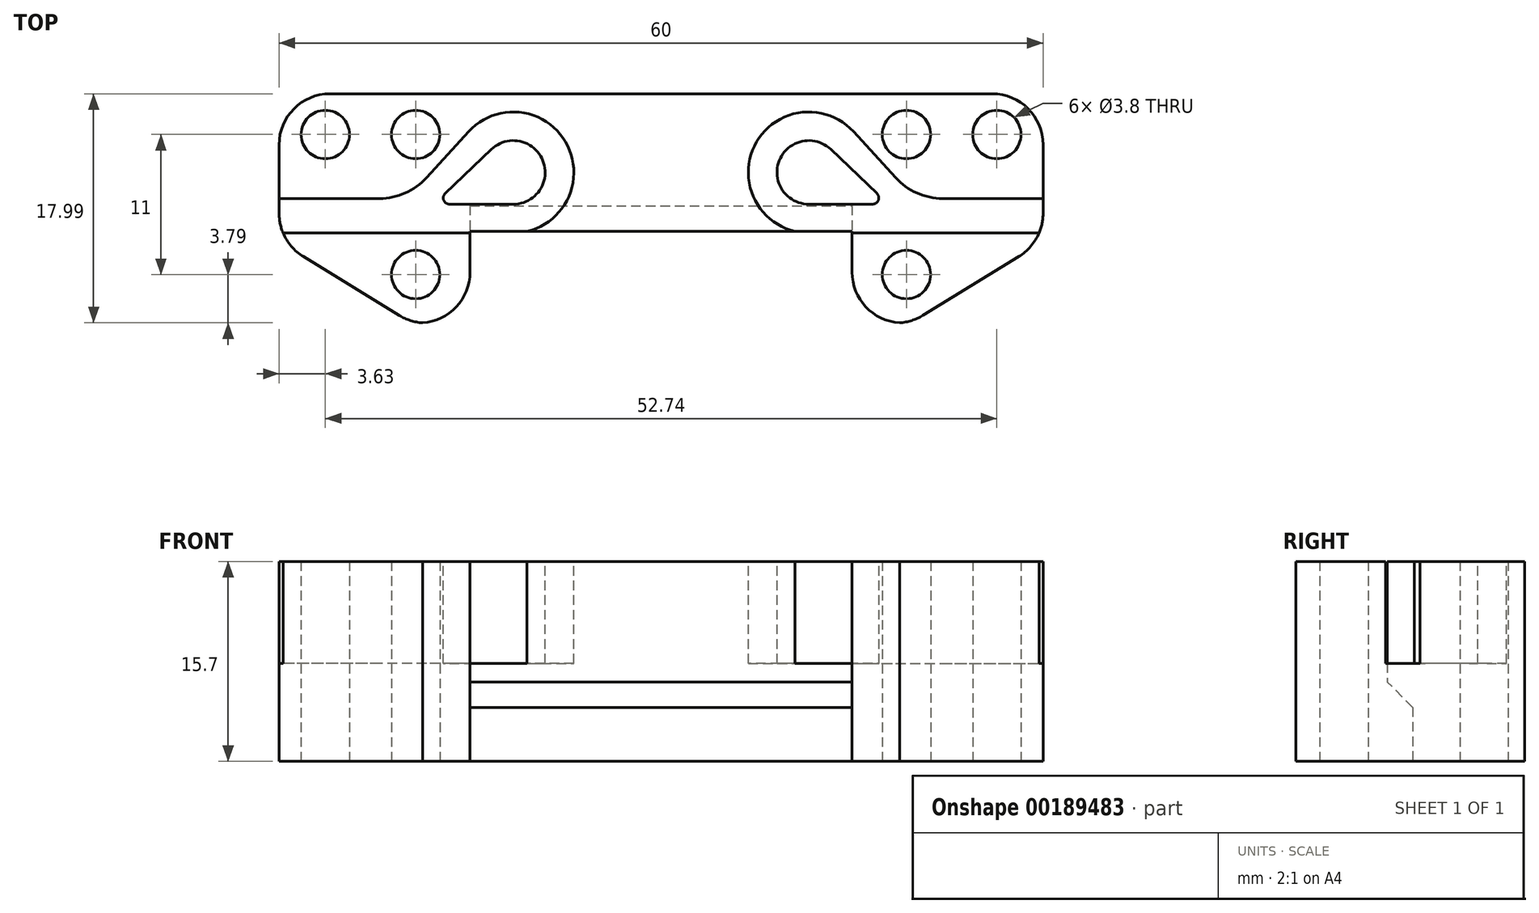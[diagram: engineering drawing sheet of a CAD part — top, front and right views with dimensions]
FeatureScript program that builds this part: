
annotation { "Feature Type Name" : "Feature", "Feature Type Description" : "" }
export const myFeature = defineFeature(function(context is Context, id is Id, definition is map)
    precondition{}
    {
        {
            var Q0;
            Q0=qCreatedBy(makeId("Top.planeOp"),FACE);
            var sketch = newSketch(context, id + "F0", { "sketchPlane" : qUnion([Q0])});
            skLineSegment(sketch, "E0.bottom", {"start": v(0, 9) * mm, "end": v(30, 9) * mm});
            skLineSegment(sketch, "E0.top", {"start": v(0, -9) * mm, "end": v(19.6, -9) * mm});
            skLineSegment(sketch, "E0.left", {"start": v(0, 9) * mm, "end": v(0, -9) * mm});
            skLineSegment(sketch, "E0.right", {"start": v(30, 9) * mm, "end": v(30, -2.62) * mm});
            skLineSegment(sketch, "E1.bottom", {"start": v(0, -1.8) * mm, "end": v(15, -1.8) * mm});
            skLineSegment(sketch, "E1.top", {"start": v(0, -9) * mm, "end": v(15, -9) * mm});
            skLineSegment(sketch, "E1.left", {"start": v(0, -1.8) * mm, "end": v(0, -9) * mm});
            skLineSegment(sketch, "E1.right", {"start": v(15, -1.8) * mm, "end": v(15, -9) * mm});
            skCircle(sketch, "E2", {"center": v(26.37, 5.8) * mm, "radius": 1.9 * mm});
            skCircle(sketch, "E3", {"center": v(19.27, 5.8) * mm, "radius": 1.9 * mm});
            skLineSegment(sketch, "E4", {"start": v(19.27, 5.8) * mm, "end": v(26.37, 5.8) * mm});
            skCircle(sketch, "E5", {"center": v(19.27, -5.2) * mm, "radius": 1.9 * mm});
            skLineSegment(sketch, "E6", {"start": v(19.27, 5.8) * mm, "end": v(19.27, -5.2) * mm});
            skLineSegment(sketch, "E7", {"start": v(19.6, -9) * mm, "end": v(30, -2.62) * mm});
            skSolve(sketch);
        }
        {
            var Q0;
            Q0=makeQuery(id+"F0.imprint","IMPRINT",FACE,{"disambiguationData":[TD([[makeQuery(id+"F0.imprint","IMPRINT",EDGE,{"derivedFrom":sQuery(id+"F0.wireOp",EDGE,"E0.bottom")}),-1.0]])]});
            extrude(context, id + "F1", {"entities" : qUnion([Q0]), "depth" : 7.85 * 2 * mm});
        }
        {
            var Q0;
            Q0=makeQuery(id+"F1.opExtrude","CAP_FACE",FACE,{"disambiguationData":[OSD([sQuery(id+"F0.wireOp",EDGE,"E0.bottom"),sQuery(id+"F0.wireOp",EDGE,"E0.top"),sQuery(id+"F0.wireOp",EDGE,"E0.left"),sQuery(id+"F0.wireOp",EDGE,"E0.right")])],"isStart":false});
            var sketch = newSketch(context, id + "F2", { "sketchPlane" : qUnion([Q0])});
            skCircle(sketch, "E8", {"center": v(11.6, 2.83) * mm, "radius": 2.5 * mm});
            skCircle(sketch, "E9", {"center": v(16.6, 0.83) * mm, "radius": 0.5 * mm});
            skLineSegment(sketch, "E10", {"start": v(13.33, 4.64) * mm, "end": v(16.95, 1.19) * mm});
            skLineSegment(sketch, "E11", {"start": v(16.6, 0.33) * mm, "end": v(11.6, 0.33) * mm});
            skCircle(sketch, "E12", {"center": v(11.6, 2.83) * mm, "radius": 4.75 * mm});
            skLineSegment(sketch, "E13.bottom", {"start": v(19.9, 0.78) * mm, "end": v(31.09, 0.78) * mm});
            skLineSegment(sketch, "E13.top", {"start": v(19.9, -1.92) * mm, "end": v(31.09, -1.92) * mm});
            skLineSegment(sketch, "E13.left", {"start": v(19.9, 0.78) * mm, "end": v(19.9, -1.92) * mm});
            skLineSegment(sketch, "E13.right", {"start": v(31.09, 0.78) * mm, "end": v(31.09, -1.92) * mm});
            skLineSegment(sketch, "E14", {"start": v(15.11, 6.03) * mm, "end": v(19.9, 0.78) * mm});
            skLineSegment(sketch, "E15", {"start": v(11.6, -1.92) * mm, "end": v(19.9, -1.92) * mm});
            skSolve(sketch);
        }
        {
            var Q0;
            {var subQ0=sQuery(id+"F2.wireOp",EDGE,"E10");var subQ1=sQuery(id+"F2.wireOp",EDGE,"E8");var subQ2=makeQuery(id+"F2.imprint","INTERSECT",VERTEX,{"derivedFrom":[subQ1,subQ0]});Q0=makeQuery(id+"F2.imprint","IMPRINT",FACE,{"disambiguationData":[TD([[makeQuery(id+"F2.imprint","IMPRINT",EDGE,{"disambiguationData":[TD([[subQ2,-1.0]])],"derivedFrom":subQ1}),-1.0]])]});}
            var Q1;
            {var subQ0=sQuery(id+"F2.wireOp",EDGE,"E12");var subQ1=sQuery(id+"F2.wireOp",EDGE,"E11");var subQ2=makeQuery(id+"F2.imprint","INTERSECT",VERTEX,{"derivedFrom":[subQ1,subQ0]});Q1=makeQuery(id+"F2.imprint","IMPRINT",FACE,{"disambiguationData":[TD([[makeQuery(id+"F2.imprint","IMPRINT",EDGE,{"disambiguationData":[TD([[subQ2,-1.0]])],"derivedFrom":subQ1}),1.0]])]});}
            var Q2;
            {var subQ5=sQuery(id+"F2.wireOp",EDGE,"E13.left");Q2=makeQuery(id+"F2.imprint","IMPRINT",FACE,{"disambiguationData":[TD([[makeQuery(id+"F2.imprint","IMPRINT",EDGE,{"derivedFrom":subQ5}),-1.0]])]});}
            var Q3;
            {var subQ0=sQuery(id+"F2.wireOp",EDGE,"E13.left");Q3=makeQuery(id+"F2.imprint","IMPRINT",FACE,{"disambiguationData":[TD([[makeQuery(id+"F2.imprint","IMPRINT",EDGE,{"derivedFrom":subQ0}),1.0]])]});}
            extrude(context, id + "F3", {"entities" : qUnion([Q0, Q1, Q2, Q3]), "operationType" : NewBodyOperationType.REMOVE, "oppositeDirection" : true, "depth" : 8 * mm});
        }
        {
            var Q0;
            Q0=makeQuery(id+"F3.boolean.opBoolean","COPY",EDGE,{"derivedFrom":makeQuery(id+"F3.opExtrude","SWEPT_EDGE",EDGE,{"disambiguationData":[OSD([sQuery(id+"F2.wireOp",EDGE,"E13.bottom"),sQuery(id+"F2.wireOp",EDGE,"E13.left"),sQuery(id+"F2.wireOp",EDGE,"E14")])]})});
            fillet(context, id + "F4", {"entities" : qUnion([Q0]), "radius" : 5 * mm, "tangentPropagation" : true, "allowEdgeOverflow" : false});
        }
        {
            var Q0;
            Q0=makeQuery(id+"F1.opExtrude","SWEPT_EDGE",EDGE,{"disambiguationData":[OSD([sQuery(id+"F0.wireOp",EDGE,"E0.right"),sQuery(id+"F0.wireOp",EDGE,"E7")])]});
            var Q1;
            Q1=makeQuery(id+"F1.opExtrude","SWEPT_EDGE",EDGE,{"disambiguationData":[OSD([sQuery(id+"F0.wireOp",EDGE,"E0.top"),sQuery(id+"F0.wireOp",EDGE,"E7")])]});
            var Q2;
            Q2=makeQuery(id+"F1.opExtrude","SWEPT_EDGE",EDGE,{"disambiguationData":[OSD([sQuery(id+"F0.wireOp",EDGE,"E0.top"),sQuery(id+"F0.wireOp",EDGE,"E1.top"),sQuery(id+"F0.wireOp",EDGE,"E1.right")])]});
            var Q3;
            Q3=makeQuery(id+"F1.opExtrude","SWEPT_EDGE",EDGE,{"disambiguationData":[OSD([sQuery(id+"F0.wireOp",EDGE,"E0.bottom"),sQuery(id+"F0.wireOp",EDGE,"E0.right")])]});
            fillet(context, id + "F5", {"entities" : qUnion([Q0, Q1, Q2, Q3]), "radius" : 4 * mm, "tangentPropagation" : true, "allowEdgeOverflow" : false});
        }
        {
            var Q0;
            Q0=makeQuery(id+"F1.opExtrude","SWEPT_FACE",FACE,{"disambiguationData":[OSD([sQuery(id+"F0.wireOp",EDGE,"E1.bottom")])]});
            var sketch = newSketch(context, id + "F6", { "sketchPlane" : qUnion([Q0])});
            skLineSegment(sketch, "E16.bottom", {"start": v(0, 0) * mm, "end": v(15, 0) * mm});
            skLineSegment(sketch, "E16.top", {"start": v(0, 6.25) * mm, "end": v(15, 6.25) * mm});
            skLineSegment(sketch, "E16.left", {"start": v(0, 0) * mm, "end": v(0, 6.25) * mm});
            skLineSegment(sketch, "E16.right", {"start": v(15, 0) * mm, "end": v(15, 6.25) * mm});
            skSolve(sketch);
        }
        {
            var Q0;
            Q0=makeQuery(id+"F6.imprint","IMPRINT",FACE,{"disambiguationData":[TD([[makeQuery(id+"F6.imprint","IMPRINT",EDGE,{"derivedFrom":sQuery(id+"F6.wireOp",EDGE,"E16.bottom")}),1.0]])]});
            extrude(context, id + "F7", {"entities" : qUnion([Q0]), "operationType" : NewBodyOperationType.REMOVE, "oppositeDirection" : true, "depth" : 2 * mm});
        }
        {
            var Q0;
            Q0=makeQuery(id+"F7.boolean.opBoolean","COPY",EDGE,{"derivedFrom":makeQuery(id+"F7.opExtrude","CAP_EDGE",EDGE,{"disambiguationData":[OSD([sQuery(id+"F6.wireOp",EDGE,"E16.top")])],"isStart":false})});
            chamfer(context, id + "F8", {"entities" : qUnion([Q0]), "width" : 2 * mm, "tangentPropagation" : true});
        }
        {
            var Q0;
            Q0=makeQuery(id+"F1.opExtrude","SWEPT_BODY",BODY,{"disambiguationData":[OSD([sQuery(id+"F0.wireOp",EDGE,"E0.bottom"),sQuery(id+"F0.wireOp",EDGE,"E0.top"),sQuery(id+"F0.wireOp",EDGE,"E0.left"),sQuery(id+"F0.wireOp",EDGE,"E0.right"),sQuery(id+"F0.wireOp",EDGE,"E1.bottom"),sQuery(id+"F0.wireOp",EDGE,"E1.right"),sQuery(id+"F0.wireOp",EDGE,"E2"),sQuery(id+"F0.wireOp",EDGE,"E3"),sQuery(id+"F0.wireOp",EDGE,"E5"),sQuery(id+"F0.wireOp",EDGE,"E7")])]});
            var Q1;
            Q1=qCreatedBy(makeId("Right.planeOp"),FACE);
            mirror(context, id + "F9", {"operationType" : NewBodyOperationType.ADD, "entities" : qUnion([Q0]), "mirrorPlane" : qUnion([Q1])});
        }
    });
